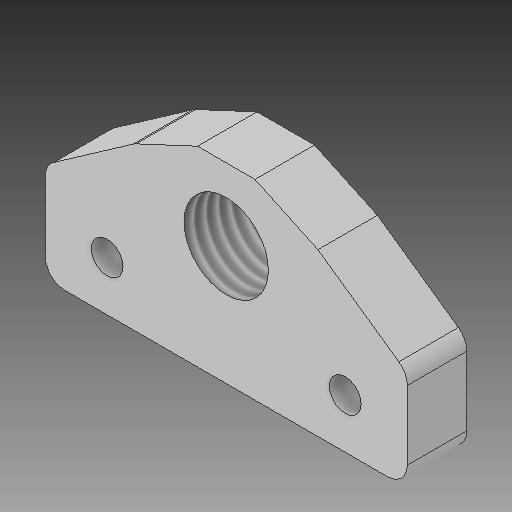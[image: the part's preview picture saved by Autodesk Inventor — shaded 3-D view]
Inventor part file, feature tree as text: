
AUTODESK INVENTOR PART (.ipt)
format: ipt  version: 2017 (Build 210142000, 142)  size: 130,560 bytes
history: native  units: mm
features: other x3, sketch x1
ambient origin geometry x8: Origin, YZ Plane, XZ Plane, XY Plane, X Axis, Y Axis, Z Axis, Center Point
bodies: Solid1 (feature_tree)
feature tree (4):
  other  "pshfit-mount-acrylic.ipt"
  other  "Solid1::pshfit-mount-acrylic.ipt"
  other  "TaggingFeature1"
  sketch  "Sketch1"  dims[d0=10.0mm]
